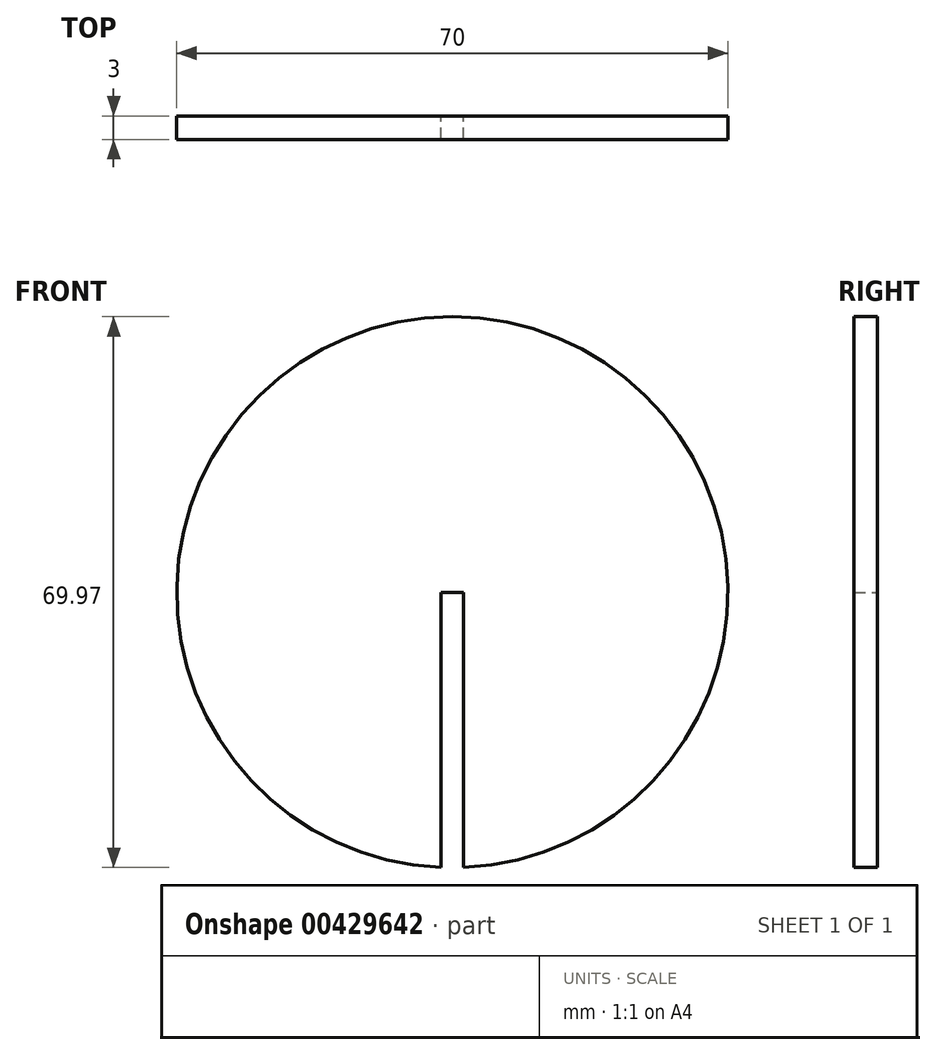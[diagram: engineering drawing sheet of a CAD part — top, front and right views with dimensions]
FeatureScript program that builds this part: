
annotation { "Feature Type Name" : "Feature", "Feature Type Description" : "" }
export const myFeature = defineFeature(function(context is Context, id is Id, definition is map)
    precondition{}
    {
        {
            var Q0;
            Q0=qCreatedBy(makeId("Front.planeOp"),FACE);
            var sketch = newSketch(context, id + "F0", { "sketchPlane" : qUnion([Q0])});
            skArc(sketch, "E0", {"start": v(1.45, -34.97) * mm, "mid": v(35, 0.73) * mm, "end": v(0, 35) * mm});
            skPoint(sketch, "E1.orphan", {"position": v(0, 35) * mm});
            skPoint(sketch, "E2.end.orphan", {"position": v(0, -35) * mm});
            skLineSegment(sketch, "E3.top", {"start": v(0, 0) * mm, "end": v(1.45, 0) * mm});
            skLineSegment(sketch, "E3.right", {"start": v(1.45, -35) * mm, "end": v(1.45, 0) * mm});
            skLineSegment(sketch, "E4.MirrorCS", {"start": v(0, 0) * mm, "end": v(-1.45, 0) * mm});
            skLineSegment(sketch, "E5.MirrorCS", {"start": v(-1.45, -35) * mm, "end": v(-1.45, 0) * mm});
            skArc(sketch, "E6.MirrorCS", {"start": v(-1.45, -34.97) * mm, "mid": v(-35, 0.73) * mm, "end": v(0, 35) * mm});
            skSolve(sketch);
        }
        {
            var Q0;
            Q0 = qSketchRegion(id + "F0", true);
            extrude(context, id + "F1", {"entities" : qUnion([Q0]), "depth" : 3 * mm});
        }
    });
